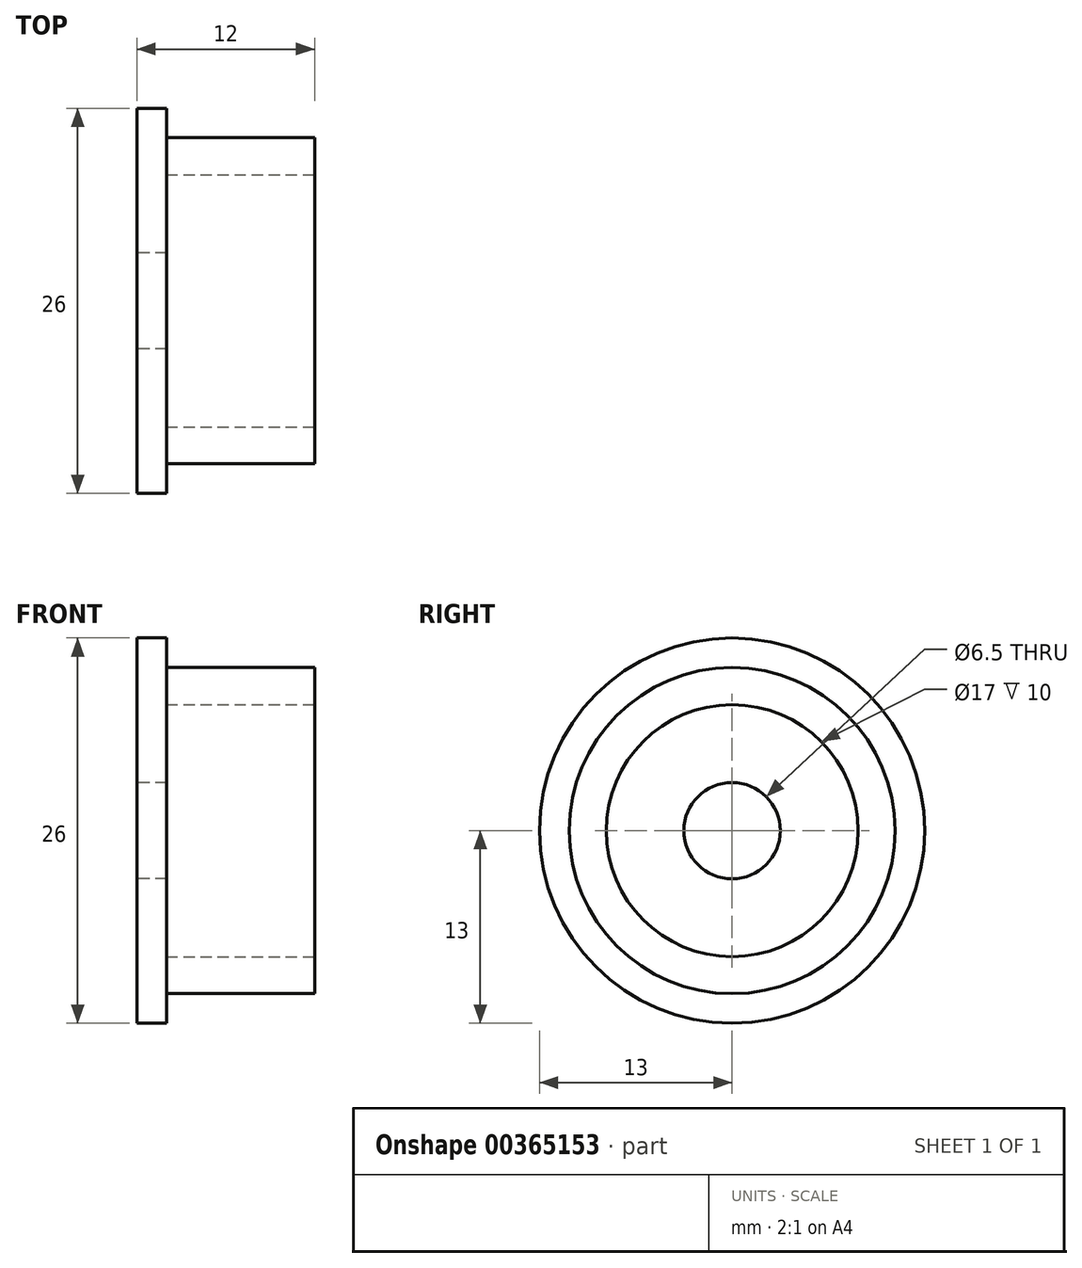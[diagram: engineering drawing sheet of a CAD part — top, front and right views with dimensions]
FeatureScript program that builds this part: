
annotation { "Feature Type Name" : "Feature", "Feature Type Description" : "" }
export const myFeature = defineFeature(function(context is Context, id is Id, definition is map)
    precondition{}
    {
        {
            var Q0;
            Q0=qCreatedBy(makeId("Right.planeOp"),FACE);
            var sketch = newSketch(context, id + "F0", { "sketchPlane" : qUnion([Q0])});
            skCircle(sketch, "E0", {"center": v(0, 0) * mm, "radius": 11 * mm});
            skCircle(sketch, "E1", {"center": v(0, 0) * mm, "radius": 9 * mm});
            skCircle(sketch, "E2", {"center": v(0, 0) * mm, "radius": 3.25 * mm});
            skCircle(sketch, "E3", {"center": v(0, 0) * mm, "radius": 13 * mm});
            skSolve(sketch);
        }
        {
            var Q0;
            Q0=makeQuery(id+"F0.imprint","IMPRINT",FACE,{"disambiguationData":[TD([[makeQuery(id+"F0.imprint","IMPRINT",EDGE,{"derivedFrom":sQuery(id+"F0.wireOp",EDGE,"E1")}),1.0]])]});
            var Q1;
            Q1=makeQuery(id+"F0.imprint","IMPRINT",FACE,{"disambiguationData":[TD([[makeQuery(id+"F0.imprint","IMPRINT",EDGE,{"derivedFrom":sQuery(id+"F0.wireOp",EDGE,"E0")}),1.0]])]});
            extrude(context, id + "F1", {"entities" : qUnion([Q0, Q1]), "depth" : 12 * mm});
        }
        {
            var Q0;
            Q0=makeQuery(id+"F1.opExtrude","CAP_FACE",FACE,{"disambiguationData":[OSD([sQuery(id+"F0.wireOp",EDGE,"E0")])],"isStart":false});
            var sketch = newSketch(context, id + "F2", { "sketchPlane" : qUnion([Q0])});
            skCircle(sketch, "E4", {"center": v(0, 0) * mm, "radius": 8.5 * mm});
            skSolve(sketch);
        }
        {
            var Q0;
            Q0=makeQuery(id+"F2.imprint","IMPRINT",FACE,{"disambiguationData":[TD([[makeQuery(id+"F2.imprint","IMPRINT",EDGE,{"derivedFrom":sQuery(id+"F2.wireOp",EDGE,"E4")}),1.0]])]});
            extrude(context, id + "F3", {"entities" : qUnion([Q0]), "operationType" : NewBodyOperationType.REMOVE, "oppositeDirection" : true, "depth" : 10 * mm});
        }
        {
            var Q0;
            Q0=makeQuery(id+"F0.imprint","IMPRINT",FACE,{"disambiguationData":[TD([[makeQuery(id+"F0.imprint","IMPRINT",EDGE,{"derivedFrom":sQuery(id+"F0.wireOp",EDGE,"E0")}),-1.0]])]});
            var Q1;
            Q1=makeQuery(id+"F0.imprint","IMPRINT",FACE,{"disambiguationData":[TD([[makeQuery(id+"F0.imprint","IMPRINT",EDGE,{"derivedFrom":sQuery(id+"F0.wireOp",EDGE,"E1")}),1.0]])]});
            var Q2;
            Q2=makeQuery(id+"F0.imprint","IMPRINT",FACE,{"disambiguationData":[TD([[makeQuery(id+"F0.imprint","IMPRINT",EDGE,{"derivedFrom":sQuery(id+"F0.wireOp",EDGE,"E0")}),1.0]])]});
            var Q3;
            Q3=makeQuery(id+"F1.opExtrude","CAP_FACE",FACE,{"disambiguationData":[OSD([sQuery(id+"F0.wireOp",EDGE,"E0"),sQuery(id+"F0.wireOp",EDGE,"E2")])],"isStart":true});
            extrude(context, id + "F4", {"entities" : qUnion([Q0, Q1, Q2, Q3]), "operationType" : NewBodyOperationType.ADD, "depth" : 2 * mm});
        }
    });
